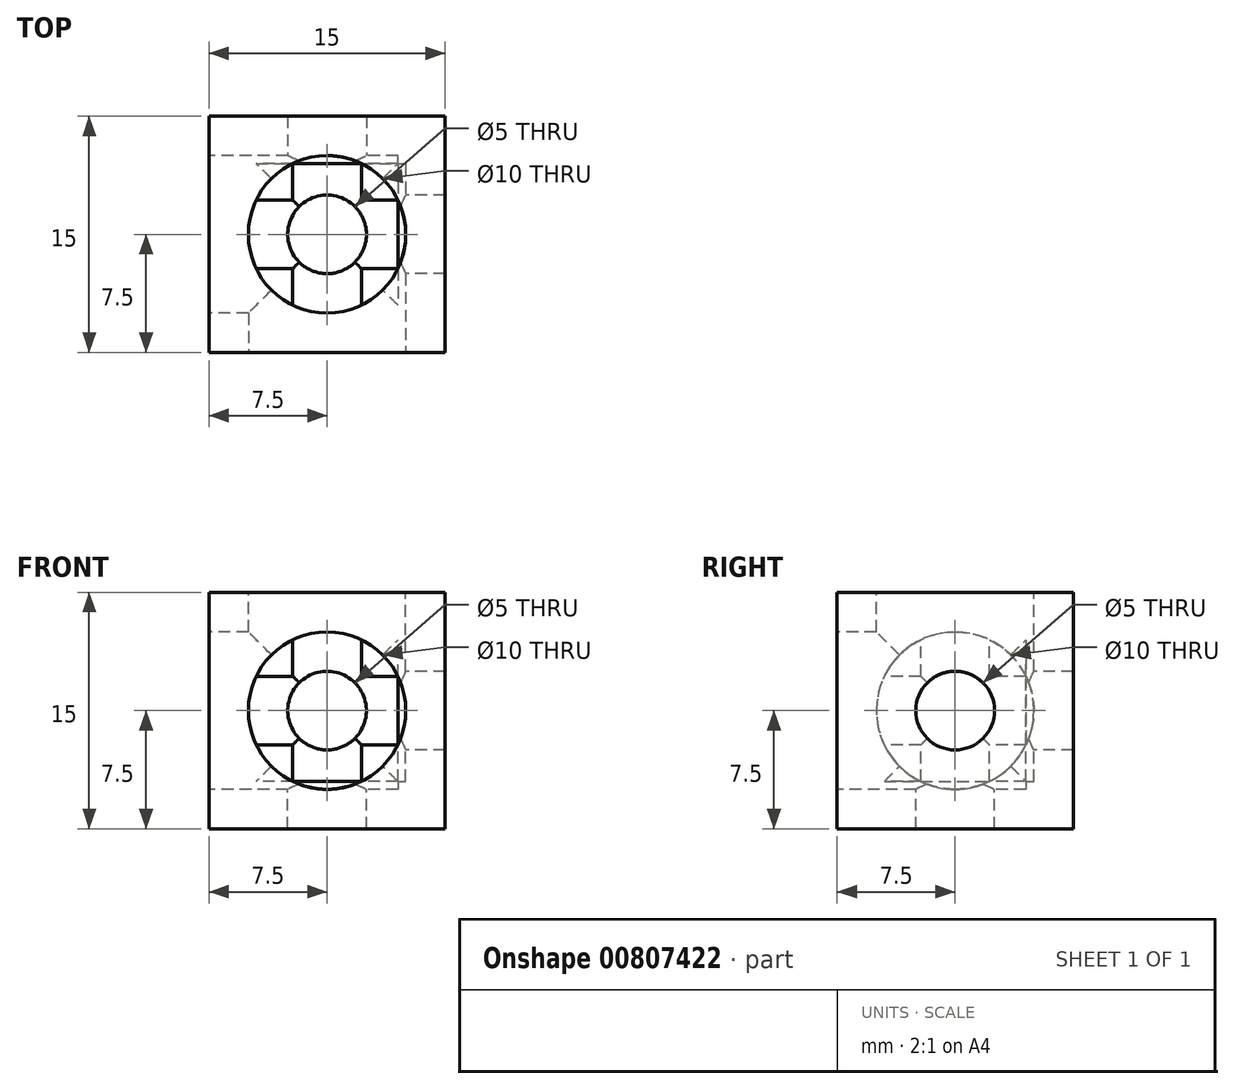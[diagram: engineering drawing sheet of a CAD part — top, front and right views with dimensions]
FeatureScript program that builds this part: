
annotation { "Feature Type Name" : "Feature", "Feature Type Description" : "" }
export const myFeature = defineFeature(function(context is Context, id is Id, definition is map)
    precondition{}
    {
        {
            var Q0;
            Q0=qCreatedBy(makeId("Top.planeOp"),FACE);
            var sketch = newSketch(context, id + "F0", { "sketchPlane" : qUnion([Q0])});
            skLineSegment(sketch, "E0.bottom", {"start": v(7.5, -7.5) * mm, "end": v(-7.5, -7.5) * mm});
            skLineSegment(sketch, "E0.top", {"start": v(7.5, 7.5) * mm, "end": v(-7.5, 7.5) * mm});
            skLineSegment(sketch, "E0.left", {"start": v(7.5, -7.5) * mm, "end": v(7.5, 7.5) * mm});
            skLineSegment(sketch, "E0.right", {"start": v(-7.5, -7.5) * mm, "end": v(-7.5, 7.5) * mm});
            skPoint(sketch, "E0.middle", {"position": v(0, 0) * mm});
            skSolve(sketch);
        }
        {
            var Q0;
            Q0 = qSketchRegion(id + "F0", true);
            extrude(context, id + "F1", {"entities" : qUnion([Q0]), "depth" : 15 * mm, "offsetDistance" : 25 * mm});
        }
        {
            var Q0;
            Q0=makeQuery(id+"F1.opExtrude","SWEPT_FACE",FACE,{"disambiguationData":[OSD([sQuery(id+"F0.wireOp",EDGE,"E0.bottom")])]});
            var sketch = newSketch(context, id + "F2", { "sketchPlane" : qUnion([Q0])});
            skPoint(sketch, "E1", {"position": v(0, 7.5) * mm});
            skPoint(sketch, "E1.positionSnap0", {"position": v(0, 0) * mm});
            skPoint(sketch, "E1.positionSnap1", {"position": v(-7.5, 7.5) * mm});
            skSolve(sketch);
        }
        {
            var Q0;
            Q0=makeQuery(id+"F1.opExtrude","SWEPT_FACE",FACE,{"disambiguationData":[OSD([sQuery(id+"F0.wireOp",EDGE,"E0.right")])]});
            var sketch = newSketch(context, id + "F3", { "sketchPlane" : qUnion([Q0])});
            skPoint(sketch, "E2", {"position": v(0, 7.5) * mm});
            skPoint(sketch, "E2.positionSnap0", {"position": v(7.5, 7.5) * mm});
            skSolve(sketch);
        }
        {
            var Q0;
            Q0=makeQuery(id+"F1.opExtrude","CAP_FACE",FACE,{"disambiguationData":[OSD([sQuery(id+"F0.wireOp",EDGE,"E0.bottom"),sQuery(id+"F0.wireOp",EDGE,"E0.top"),sQuery(id+"F0.wireOp",EDGE,"E0.left"),sQuery(id+"F0.wireOp",EDGE,"E0.right")])],"isStart":false});
            var sketch = newSketch(context, id + "F4", { "sketchPlane" : qUnion([Q0])});
            skPoint(sketch, "E3", {"position": v(0, 0) * mm});
            skSolve(sketch);
        }
        {
            var Q0;
            Q0=sQuery(id+"F2.wireOp",VERTEX,"E1");
            var Q1;
            Q1=sQuery(id+"F3.wireOp",VERTEX,"E2");
            var Q2;
            Q2=sQuery(id+"F4.wireOp",VERTEX,"E3");
            var Q3;
            Q3=makeQuery(id+"F1.opExtrude","SWEPT_BODY",BODY,{"disambiguationData":[OSD([sQuery(id+"F0.wireOp",EDGE,"E0.bottom"),sQuery(id+"F0.wireOp",EDGE,"E0.top"),sQuery(id+"F0.wireOp",EDGE,"E0.left"),sQuery(id+"F0.wireOp",EDGE,"E0.right")])]});
            hole(context, id + "F5", {"style" : HoleStyle.C_BORE, "endStyle" : HoleEndStyle.THROUGH, "holeDiameter" : 5 * mm, "cBoreDiameter" : 10 * mm, "cBoreDepth" : 12 * mm, "majorDiameter" : 5 * mm, "isTappedThrough" : true, "tappedDepth" : 12 * mm, "tapClearance" : 3, "locations" : qUnion([Q0, Q1, Q2]), "scope" : qUnion([Q3])});
        }
    });
